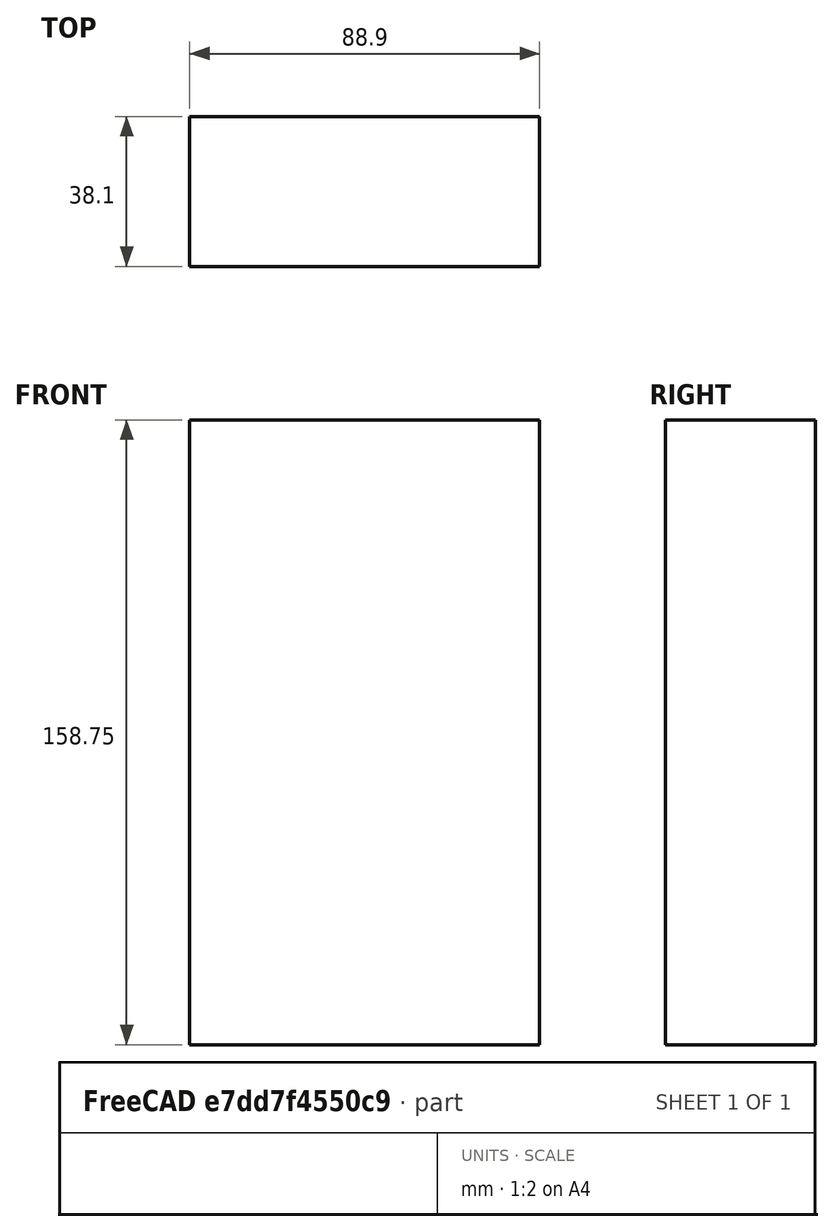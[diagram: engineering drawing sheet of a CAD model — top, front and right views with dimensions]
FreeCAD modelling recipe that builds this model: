
FCSTD DOCUMENT  (FreeCAD 0.15R4671 (Git))
Label: wb_bottom_stud
License: All rights reserved
LicenseURL: http://en.wikipedia.org/wiki/All_rights_reserved
objects: Sketcher::SketchObject×1, Part::Extrusion×1
note: 2 computed .brp shape members not serialized (recipe doc carries the construction recipe); baked Part::Feature solids carry a one-line shape summary decoded from their .brp

FEATURE [Sketcher::SketchObject] Sketch
  sketch-geometry (4):
    g0: LineSegment StartX=0 StartY=0 StartZ=0 EndX=88.9 EndY=0 EndZ=0
    g1: LineSegment StartX=88.9 StartY=0 StartZ=0 EndX=88.9 EndY=38.1 EndZ=0
    g2: LineSegment StartX=88.9 StartY=38.1 StartZ=0 EndX=0 EndY=38.1 EndZ=0
    g3: LineSegment StartX=0 StartY=38.1 StartZ=0 EndX=0 EndY=0 EndZ=0
  constraints (11):
    c: Coincident(g0,g1)
    c: Coincident(g1,g2)
    c: Coincident(g2,g3)
    c: Coincident(g3,g0)
    c: Horizontal(g0)
    c: Horizontal(g2)
    c: Vertical(g1)
    c: Vertical(g3)
    c: Coincident(g0,g-1)
    c: Distance(g3) = 38.1
    c: Distance(g0) = 88.9
FEATURE [Part::Extrusion] Extrude
  Base = -> Sketch
  Dir = (0,0,158.75)
  Solid = true
